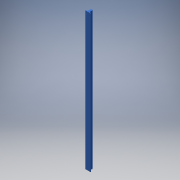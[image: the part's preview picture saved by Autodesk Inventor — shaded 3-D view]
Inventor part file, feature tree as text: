
AUTODESK INVENTOR PART (.ipt)
format: ipt  version: 2018 (Build 220112000, 112)  size: 142,336 bytes
history: native  units: mm
features: sketch x2, other x1, extrude x1, hole x1
ambient origin geometry x8: Origin, YZ Plane, XZ Plane, XY Plane, X Axis, Y Axis, Z Axis, Center Point
bodies: Body1 (feature_tree)
feature tree (5):
  other  "Sólido1"
  extrude  "Extrusão1"  Depth=25.0mm
  hole  "Furo1"  [1 undecoded]
  sketch  "Esboço1"  dims[d6=16.0mm d7=25.0mm]
  sketch  "Esboço3"  dims[d8=18.5mm d9=11.7mm d10=8.0mm d11=30.0deg d12=30.0deg d13=5.0mm d14=40.0mm d15=1054.0mm d16=0.0mm d18=15.0mm d19=15.0mm d20=5.5mm d21=5.5mm d22=20.0mm d28=5.5mm d29=6.0mm d30=4.0mm d31=2.0mm d32=90.0deg d33=8.0mm d34=20.594885mm]
note: 1 required parameter value undecoded (feature->parameter linkage not recoverable at this tier; creation-order binding heuristic only, values carry confidence <= 0.55)
